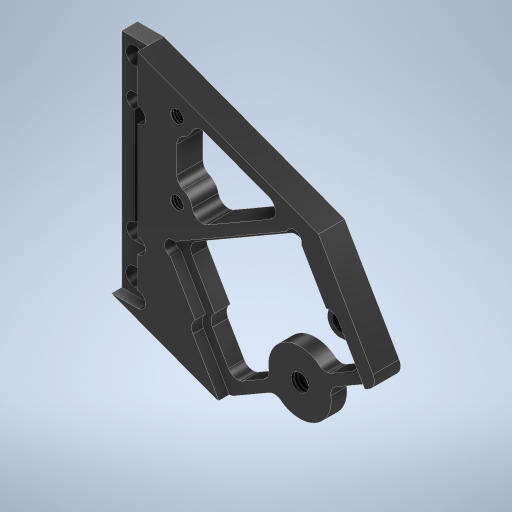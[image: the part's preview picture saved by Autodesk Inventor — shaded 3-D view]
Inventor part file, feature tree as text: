
AUTODESK INVENTOR PART (.ipt)
format: ipt  version: 2024.2 (Build 282272000, 272)  size: 439,296 bytes
history: native  units: mm
features: extrude x2, fillet x2, hole x2, other x1, sketch x1
ambient origin geometry x8: Origin, YZ Plane, XZ Plane, XY Plane, X Axis, Y Axis, Z Axis, Center Point
bodies: Solid1 (feature_tree)
feature tree (8):
  other  "ShoulderSideFrameBasis.ipt"
  extrude  "Extrusion1"  Depth=5.0mm TaperAngle=0.0deg
  extrude  "Extrusion2"  Depth=2.0mm TaperAngle=0.0deg
  fillet  "Inner-R2"  Radius=2.0mm
  fillet  "Outer-R2"  Radius=2.0mm
  hole  "Phi3.1"  [1 undecoded]
  hole  "Phi3.5"  [1 undecoded]
  sketch  "Sketch1"  dims[d0=10.0mm d1=5.0mm d2=0.0mm d3=2.0mm d4=0.0mm d5=2.0mm d6=3.242mm d7=8.0mm d8=4.0mm d9=2.0mm d10=90.0deg d11=8.0mm d12=20.594885mm d13=3.1mm d14=8.0mm d15=4.0mm d16=2.0mm d17=90.0deg d18=8.0mm d19=20.594885mm d20=3.5mm d21=6.0mm d22=4.0mm d23=2.0mm d24=90.0deg d25=8.0mm d26=20.594885mm d27=2.0mm d28=2.459mm d29=6.0mm d30=4.0mm d31=2.0mm d32=90.0deg d33=8.0mm d34=20.594885mm d35=0.5mm d36=0.872665mm d37=0.5mm d38=0.872665mm]
note: 2 required parameter values undecoded (feature->parameter linkage not recoverable at this tier; creation-order binding heuristic only, values carry confidence <= 0.55)
